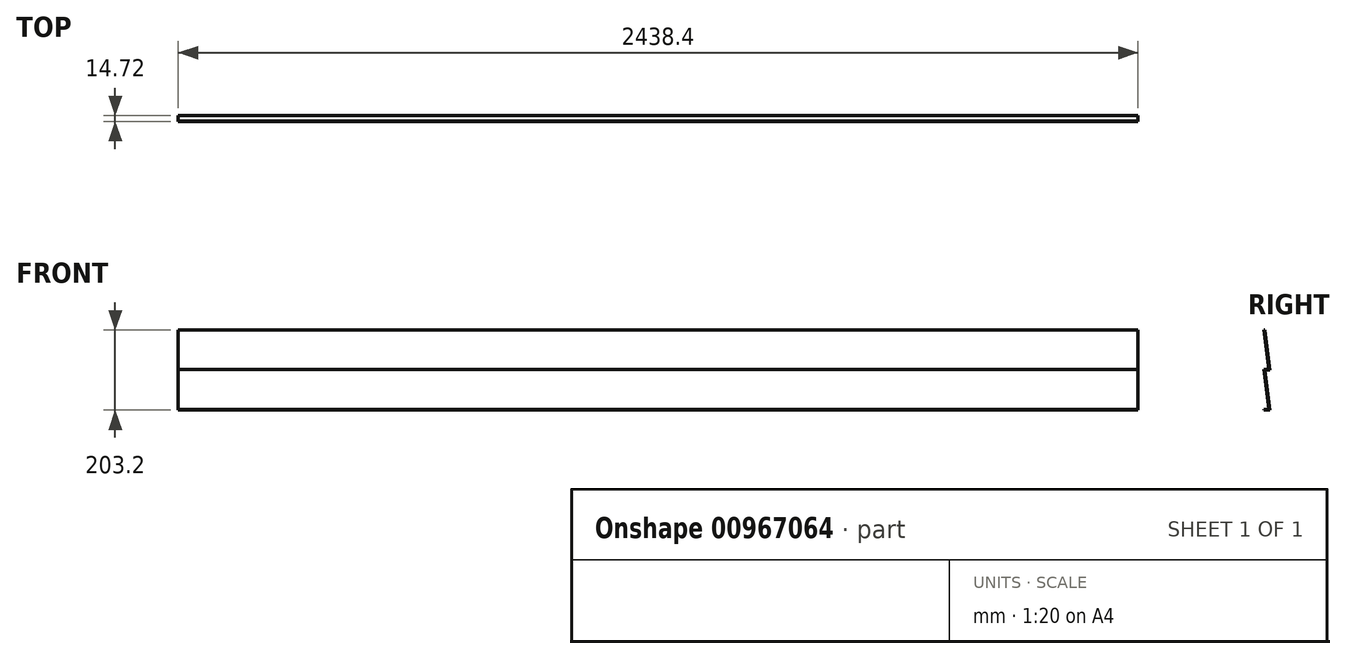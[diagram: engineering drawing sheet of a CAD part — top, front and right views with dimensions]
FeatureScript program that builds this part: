
annotation { "Feature Type Name" : "Feature", "Feature Type Description" : "" }
export const myFeature = defineFeature(function(context is Context, id is Id, definition is map)
    precondition{}
    {
        {
            var Q0;
            Q0=qCreatedBy(makeId("Right.planeOp"),FACE);
            var sketch = newSketch(context, id + "F0", { "sketchPlane" : qUnion([Q0])});
            skLineSegment(sketch, "E0", {"start": v(0, 0) * mm, "end": v(12.7, -99.82) * mm});
            skLineSegment(sketch, "E1", {"start": v(12.7, -99.82) * mm, "end": v(0, -99.82) * mm});
            skLineSegment(sketch, "E2", {"start": v(0, -99.82) * mm, "end": v(12.7, -201.42) * mm});
            skLineSegment(sketch, "E3", {"start": v(12.7, -201.42) * mm, "end": v(0, -201.42) * mm});
            skLineSegment(sketch, "E4.0", {"start": v(14.71, -203.2) * mm, "end": v(0, -203.2) * mm});
            skLineSegment(sketch, "E4.1", {"start": v(2.01, -101.6) * mm, "end": v(14.71, -203.2) * mm});
            skLineSegment(sketch, "E4.2", {"start": v(14.72, -101.6) * mm, "end": v(2.01, -101.6) * mm});
            skLineSegment(sketch, "E4.3", {"start": v(1.8, 0) * mm, "end": v(14.72, -101.6) * mm});
            skLineSegment(sketch, "E5", {"start": v(1.8, 0) * mm, "end": v(0, 0) * mm});
            skLineSegment(sketch, "E6", {"start": v(0, -201.42) * mm, "end": v(0, -203.2) * mm});
            skSolve(sketch);
        }
        {
            var Q0;
            Q0 = qSketchRegion(id + "F0", true);
            extrude(context, id + "F1", {"entities" : qUnion([Q0]), "depth" : 2438.4 * mm, "offsetDistance" : 25.4 * mm});
        }
    });
